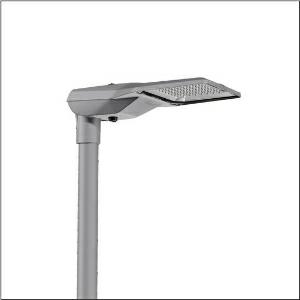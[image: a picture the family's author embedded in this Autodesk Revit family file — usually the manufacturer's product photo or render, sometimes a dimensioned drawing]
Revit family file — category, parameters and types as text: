
# Revit family: streetlight_sl_21_midi___st0_5a_5xe3b33t08nb_f8ff
name_source: partatom
category: Lighting Fixtures
units: mm (PartAtom-declared; Revit-internal decimal feet)

## family parameters
Cut with Voids When Loaded = No
Host = Face
Light Source = No
Part Type = Normal
Room Calculation Point = No
Round Connector Dimension = Use Diameter
Shared = No

## types (1)
- --- (1 x LED, 22700 lm, 151.2 W, 3000K)
    Apparent Load = 151 VA
    CIE Flux Codes = 43 76 97 100 100
    Color Rendering = 70
    Color Temperature = 3000K
    Default Elevation = 1800 mm
    Description = Streetlight SL 21 midi, mast luminaire, primary light control with lens, of PMMA, primary optical cover: cover, of toughened safety glass, transparent, light distribution: ST0.5a, light emission: direct distribution, primary light characteristic: asymmetric, installation type: side-entry, post-top, LED, High Power LED, rated luminous flux: 22.700lm, luminous efficacy: 150lm/W, light colour: 730, colour temperature: 3000K, control gear: D4i, control: overheat protection, constant luminous flux control, time-dependent luminous flux control, flexible luminous flux parameterisation, pre-setting: logarithmic dimming characteristic, mains connection: 230..240V, AC, 50/60Hz, start of lifetime: 151W, end of service life: 157W, reduction: 70W, luminaire housing, of diecast aluminium, powder-coated, Siteco® metallic grey (DB 702S), corrosivity category C5 mid according to DIN EN ISO 12944, please order mast flange separately, inclination adjustable: 0°, 5°, 10°, 15°, sealing non-destructively replaceable, multi-level sealing system, length: 644mm, width: 335mm, height: 110mm, mast flange for spigot size: 42mm (side-entry): 5XC10008XM4, 60/48mm (side-entry/post-top): 5XC10108XM2, 76/60mm (side-entry/post-top): 5XC10108XM1, mounting height: 4..8m, Smart Interface below and above, protection rating (complete): IP66, insulation class (complete): insulation class II (safety insulation), certification: CE, ENEC, ENEC+, VDE, impact resistance: IK10, permissible operating ambient temperature for outdoor applications: -40..+50°C, standard-compliant lighting for roads and squares, packaging unit: 1 piece

Light Distribution: ST0.5a
    Height = 111 mm
    Lamp = 1 x LED
    Lamp Light Flux = 22700 lm
    Lamp Power = 151.2 W
    Lamp count = 1
    Length = 644 mm
    Luminous efficacy = 150 lm/W
    Manufacturer = Siteco
    ModVariant = No
    Model = 5XE3B33T08NB
    Number of Poles = 1
    OnlyDefault = Yes
    Power Factor = 1
    Product Name = Streetlight SL 21 midi | ST0.5a
    Product group = mast luminaire | pylon top
    ProductGroupID = 6100
    Protection Class = Protection class II
    Protection Degree = IP 66
    RLX_Detail_Level = 1
    RLX_Emergency_Light_Flux = 0 lm
    RLX_Emergency_Type = 0
    RLX_Emergency_Type_DB = No
    RlxData = <blob elided: 38209 chars, md5=2742c4ee>
    Socket = socket
    Standby Power = 0 W
    System Light Flux = 22700 lm
    System Power = 151 W
    Type Comments = factory setting: luminous flux: 100 % | dim-lin: 254 | 802 mA
    Type Image = l_1004304.jpg
    URL = http://relux.com
    VarID = @adj_171352
    Voltage = 0 V
    Weight = 0.00 kg
    Width = 336 mm

## geometry (parser evidence)
native form markers: Blend x4, Sweep x9
no freeform markers — native parametric forms only
